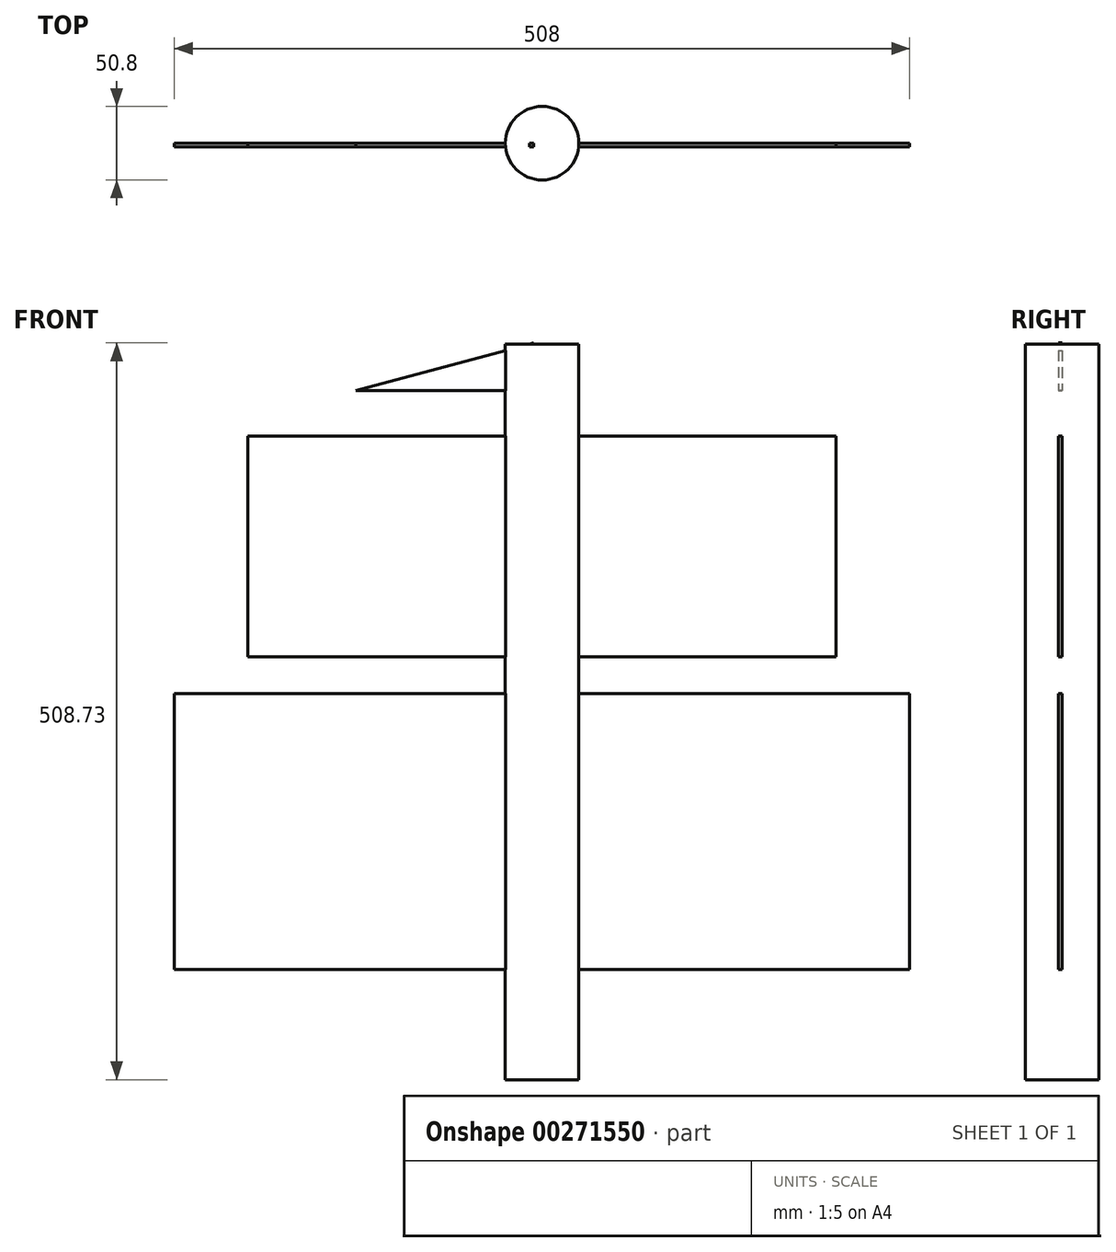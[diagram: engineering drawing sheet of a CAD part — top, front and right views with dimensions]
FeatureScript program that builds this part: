
annotation { "Feature Type Name" : "Feature", "Feature Type Description" : "" }
export const myFeature = defineFeature(function(context is Context, id is Id, definition is map)
    precondition{}
    {
        {
            var Q0;
            Q0=qCreatedBy(makeId("Front.planeOp"),FACE);
            var sketch = newSketch(context, id + "F0", { "sketchPlane" : qUnion([Q0])});
            skLineSegment(sketch, "E0", {"start": v(0, -56.68) * mm, "end": v(0, 451.32) * mm});
            skLineSegment(sketch, "E1", {"start": v(0, 451.32) * mm, "end": v(25.4, 451.32) * mm});
            skLineSegment(sketch, "E2", {"start": v(25.4, 451.32) * mm, "end": v(25.4, -56.68) * mm});
            skLineSegment(sketch, "E3", {"start": v(25.4, -56.68) * mm, "end": v(0, -56.68) * mm});
            skSolve(sketch);
        }
        {
            var Q0;
            Q0=makeQuery(id+"F0.imprint","IMPRINT",FACE,{"disambiguationData":[TD([[makeQuery(id+"F0.imprint","IMPRINT",EDGE,{"derivedFrom":sQuery(id+"F0.wireOp",EDGE,"E0")}),-1.0]])]});
            var Q1;
            Q1=sQuery(id+"F0.wireOp",EDGE,"E0");
            revolve(context, id + "F1", {"entities" : qUnion([Q0]), "axis" : qUnion([Q1]), "revolveType" : RevolveType.FULL});
        }
        {
            var Q0;
            Q0=qCreatedBy(makeId("Front.planeOp"),FACE);
            var sketch = newSketch(context, id + "F2", { "sketchPlane" : qUnion([Q0])});
            skLineSegment(sketch, "E4.bottom", {"start": v(-254, 210.02) * mm, "end": v(254, 210.02) * mm});
            skLineSegment(sketch, "E4.top", {"start": v(-254, 19.52) * mm, "end": v(254, 19.52) * mm});
            skLineSegment(sketch, "E4.left", {"start": v(-254, 210.02) * mm, "end": v(-254, 19.52) * mm});
            skLineSegment(sketch, "E4.right", {"start": v(254, 210.02) * mm, "end": v(254, 19.52) * mm});
            skPoint(sketch, "E4.middle", {"position": v(0, 114.77) * mm});
            skSolve(sketch);
        }
        {
            var Q0;
            Q0 = qSketchRegion(id + "F2", true);
            extrude(context, id + "F3", {"entities" : qUnion([Q0]), "operationType" : NewBodyOperationType.ADD, "depth" : 2.54 * mm});
        }
        {
            var Q0;
            Q0=qCreatedBy(makeId("Front.planeOp"),FACE);
            var sketch = newSketch(context, id + "F4", { "sketchPlane" : qUnion([Q0])});
            skLineSegment(sketch, "E5.bottom", {"start": v(-203.2, 387.82) * mm, "end": v(203.2, 387.82) * mm});
            skLineSegment(sketch, "E5.top", {"start": v(-203.2, 235.42) * mm, "end": v(203.2, 235.42) * mm});
            skLineSegment(sketch, "E5.left", {"start": v(-203.2, 387.82) * mm, "end": v(-203.2, 235.42) * mm});
            skLineSegment(sketch, "E5.right", {"start": v(203.2, 387.82) * mm, "end": v(203.2, 235.42) * mm});
            skPoint(sketch, "E5.middle", {"position": v(0, 311.62) * mm});
            skLineSegment(sketch, "E6", {"start": v(-6.02, 452.05) * mm, "end": v(-128.65, 419.03) * mm});
            skLineSegment(sketch, "E7", {"start": v(-128.65, 419.03) * mm, "end": v(-6.02, 419.03) * mm});
            skLineSegment(sketch, "E8", {"start": v(-6.02, 419.03) * mm, "end": v(-6.02, 452.05) * mm});
            skSolve(sketch);
        }
        {
            var Q0;
            Q0 = qSketchRegion(id + "F4", true);
            extrude(context, id + "F5", {"entities" : qUnion([Q0]), "operationType" : NewBodyOperationType.ADD, "depth" : 2.54 * mm});
        }
    });
